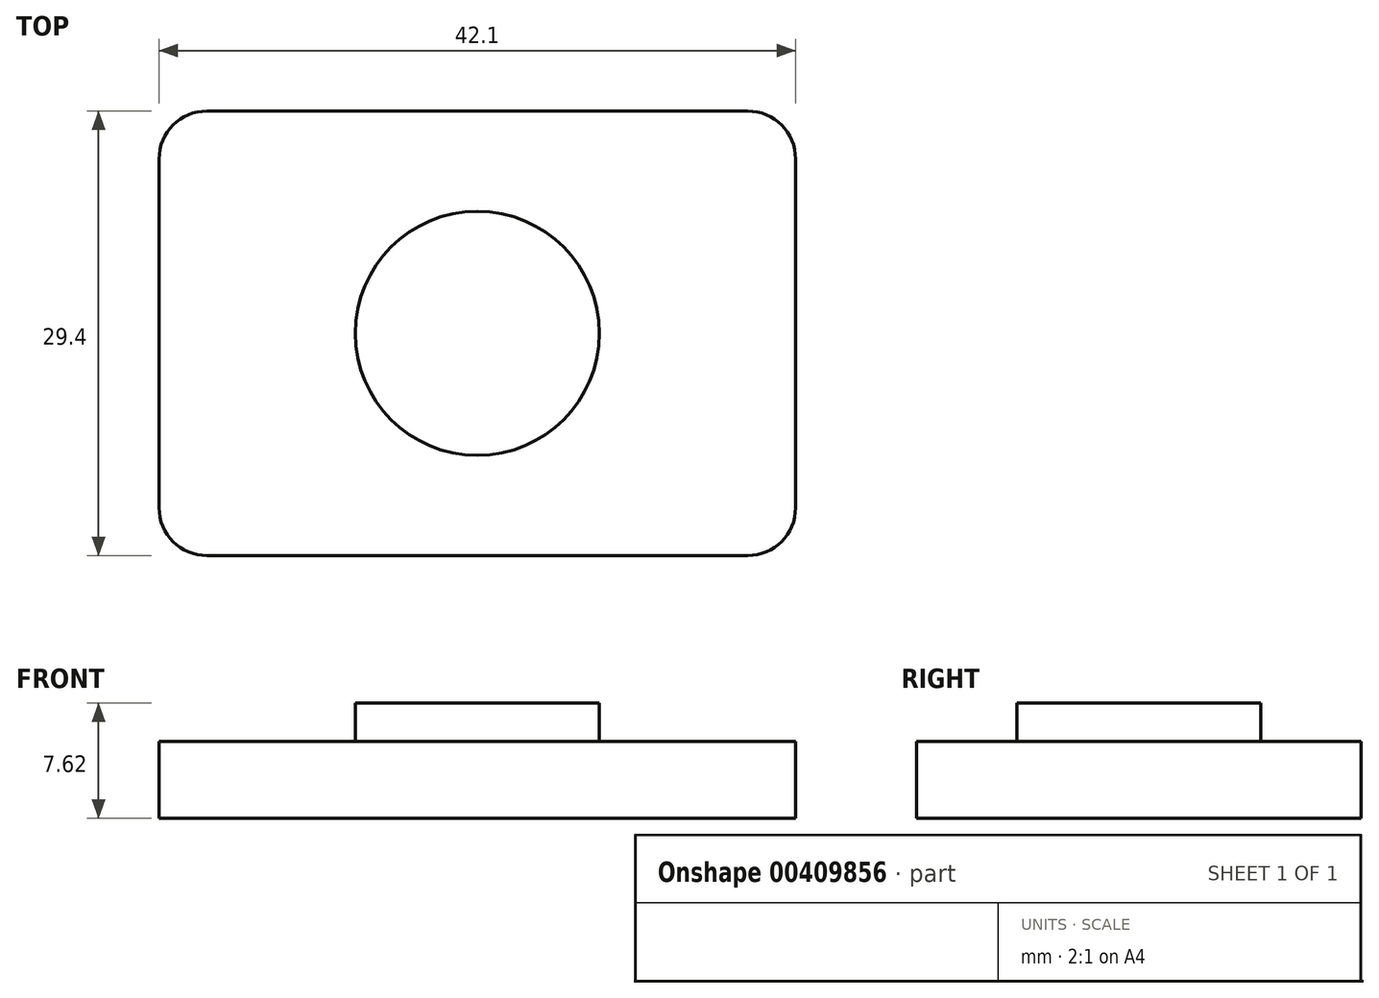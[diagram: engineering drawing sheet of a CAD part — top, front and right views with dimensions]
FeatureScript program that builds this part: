
annotation { "Feature Type Name" : "Feature", "Feature Type Description" : "" }
export const myFeature = defineFeature(function(context is Context, id is Id, definition is map)
    precondition{}
    {
        {
            var Q0;
            Q0=qCreatedBy(makeId("Top.planeOp"),FACE);
            var sketch = newSketch(context, id + "F0", { "sketchPlane" : qUnion([Q0])});
            skLineSegment(sketch, "E0.bottom", {"start": v(17.88, 14.7) * mm, "end": v(-17.88, 14.7) * mm});
            skLineSegment(sketch, "E0.top", {"start": v(17.88, -14.7) * mm, "end": v(-17.88, -14.7) * mm});
            skLineSegment(sketch, "E0.left", {"start": v(21.05, 11.53) * mm, "end": v(21.05, -11.52) * mm});
            skLineSegment(sketch, "E0.right", {"start": v(-21.05, 11.53) * mm, "end": v(-21.05, -11.52) * mm});
            skPoint(sketch, "E0.middle", {"position": v(0, 0) * mm});
            skPoint(sketch, "E1.visualSharp", {"position": v(21.05, 14.7) * mm});
            skArc(sketch, "E1.filletArc", {"start": v(21.05, 11.53) * mm, "mid": v(20.12, 13.77) * mm, "end": v(17.88, 14.7) * mm});
            skPoint(sketch, "E2.visualSharp", {"position": v(-21.05, 14.7) * mm});
            skArc(sketch, "E2.filletArc", {"start": v(-17.88, 14.7) * mm, "mid": v(-20.12, 13.77) * mm, "end": v(-21.05, 11.53) * mm});
            skPoint(sketch, "E3.visualSharp", {"position": v(-21.05, -14.7) * mm});
            skArc(sketch, "E3.filletArc", {"start": v(-21.05, -11.52) * mm, "mid": v(-20.12, -13.77) * mm, "end": v(-17.88, -14.7) * mm});
            skPoint(sketch, "E4.visualSharp", {"position": v(21.05, -14.7) * mm});
            skArc(sketch, "E4.filletArc", {"start": v(17.88, -14.7) * mm, "mid": v(20.12, -13.77) * mm, "end": v(21.05, -11.52) * mm});
            skSolve(sketch);
        }
        {
            var Q0;
            Q0 = qSketchRegion(id + "F0", true);
            extrude(context, id + "F1", {"entities" : qUnion([Q0]), "depth" : 5.08 * mm});
        }
        {
            var Q0;
            Q0=makeQuery(id+"F1.opExtrude","CAP_FACE",FACE,{"disambiguationData":[OSD([sQuery(id+"F0.wireOp",EDGE,"E0.bottom"),sQuery(id+"F0.wireOp",EDGE,"E0.top"),sQuery(id+"F0.wireOp",EDGE,"E0.left"),sQuery(id+"F0.wireOp",EDGE,"E0.right"),sQuery(id+"F0.wireOp",EDGE,"E1.filletArc"),sQuery(id+"F0.wireOp",EDGE,"E2.filletArc"),sQuery(id+"F0.wireOp",EDGE,"E3.filletArc"),sQuery(id+"F0.wireOp",EDGE,"E4.filletArc")])],"isStart":false});
            var sketch = newSketch(context, id + "F2", { "sketchPlane" : qUnion([Q0])});
            skCircle(sketch, "E5", {"center": v(0, 0) * mm, "radius": 8.07 * mm});
            skSolve(sketch);
        }
        {
            var Q0;
            Q0 = qSketchRegion(id + "F2", true);
            extrude(context, id + "F3", {"entities" : qUnion([Q0]), "operationType" : NewBodyOperationType.ADD, "depth" : 2.54 * mm});
        }
    });
